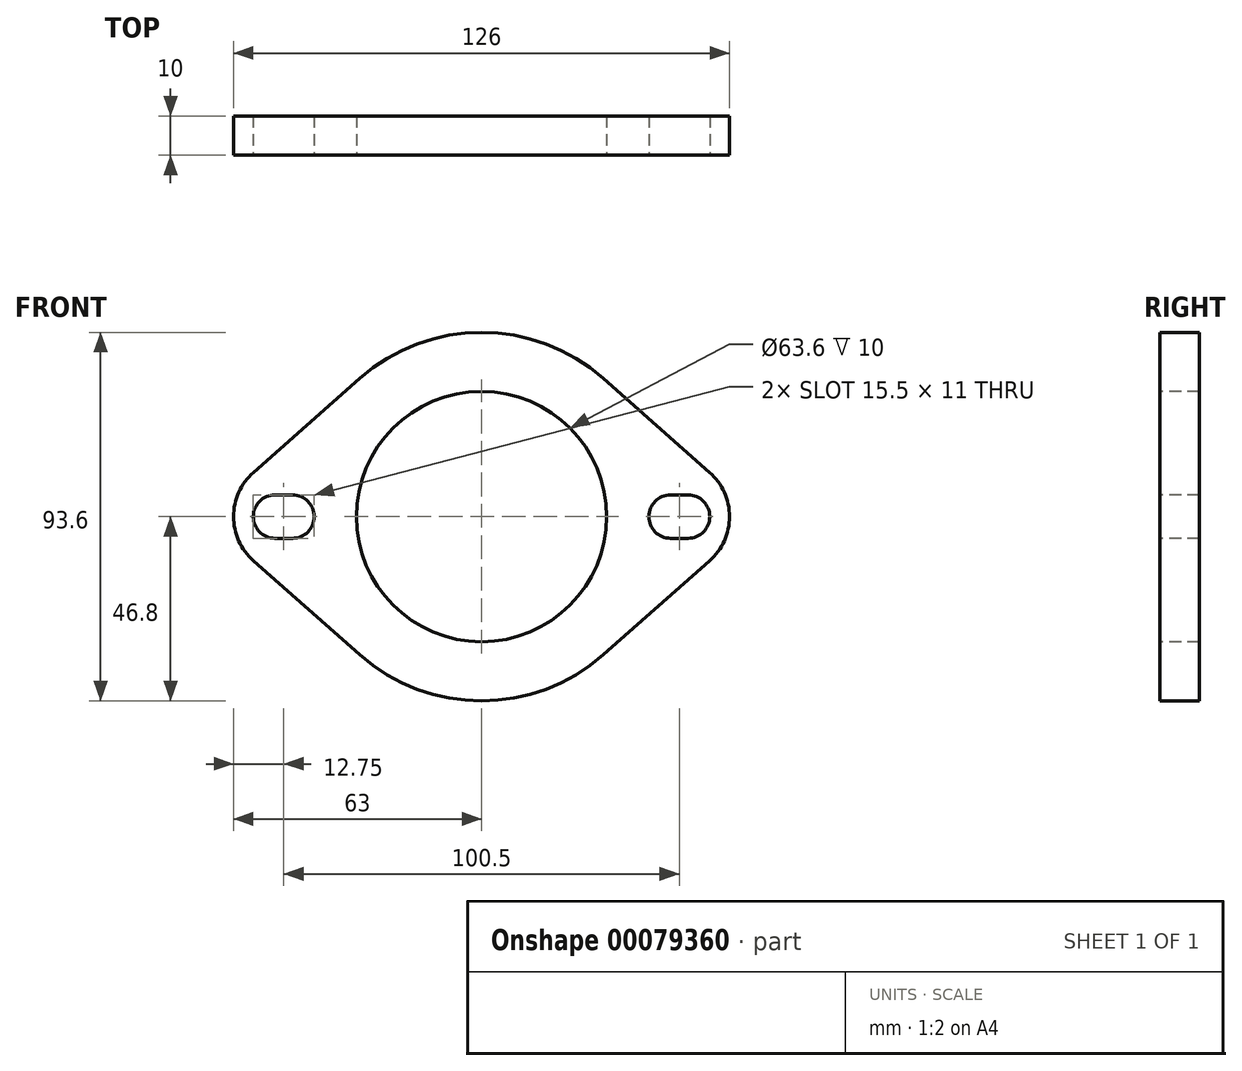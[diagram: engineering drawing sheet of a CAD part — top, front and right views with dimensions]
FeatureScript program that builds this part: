
annotation { "Feature Type Name" : "Feature", "Feature Type Description" : "" }
export const myFeature = defineFeature(function(context is Context, id is Id, definition is map)
    precondition{}
    {
        {
            var Q0;
            Q0=qCreatedBy(makeId("Front.planeOp"),FACE);
            var sketch = newSketch(context, id + "F0", { "sketchPlane" : qUnion([Q0])});
            skCircle(sketch, "E0", {"center": v(73, 56.8) * mm, "radius": 31.8 * mm});
            skArc(sketch, "E1", {"start": v(42, 21.74) * mm, "mid": v(73, 10) * mm, "end": v(104, 21.74) * mm});
            skArc(sketch, "E2", {"start": v(15.06, 68.04) * mm, "mid": v(10, 56.8) * mm, "end": v(15.06, 45.56) * mm});
            skArc(sketch, "E3", {"start": v(130.94, 45.56) * mm, "mid": v(136, 56.8) * mm, "end": v(130.94, 68.04) * mm});
            skLineSegment(sketch, "E4", {"start": v(15.06, 68.04) * mm, "end": v(42, 91.86) * mm});
            skLineSegment(sketch, "E5", {"start": v(15.06, 45.56) * mm, "end": v(42, 21.74) * mm});
            skLineSegment(sketch, "E6", {"start": v(130.94, 68.04) * mm, "end": v(104, 91.86) * mm});
            skLineSegment(sketch, "E7", {"start": v(130.94, 45.56) * mm, "end": v(104, 21.74) * mm});
            skArc(sketch, "E8.trimOffspring", {"start": v(104, 91.86) * mm, "mid": v(73, 103.6) * mm, "end": v(42, 91.86) * mm});
            skArc(sketch, "E9", {"start": v(25, 51.3) * mm, "mid": v(30.5, 56.8) * mm, "end": v(25, 62.3) * mm});
            skArc(sketch, "E10", {"start": v(20.5, 62.3) * mm, "mid": v(15, 56.8) * mm, "end": v(20.5, 51.3) * mm});
            skLineSegment(sketch, "E11", {"start": v(20.5, 51.3) * mm, "end": v(25, 51.3) * mm});
            skArc(sketch, "E12.MirrorCS", {"start": v(121, 51.3) * mm, "mid": v(115.5, 56.8) * mm, "end": v(121, 62.3) * mm});
            skArc(sketch, "E13.MirrorCS", {"start": v(125.5, 62.3) * mm, "mid": v(131, 56.8) * mm, "end": v(125.5, 51.3) * mm});
            skLineSegment(sketch, "E14", {"start": v(20.5, 62.3) * mm, "end": v(25, 62.3) * mm});
            skLineSegment(sketch, "E15", {"start": v(121, 62.3) * mm, "end": v(125.5, 62.3) * mm});
            skLineSegment(sketch, "E16", {"start": v(121, 51.3) * mm, "end": v(125.5, 51.3) * mm});
            skLineSegment(sketch, "E17", {"start": v(0, 0) * mm, "end": v(0, 82.13) * mm});
            skLineSegment(sketch, "E18", {"start": v(0, 0) * mm, "end": v(145.22, 0) * mm});
            skSolve(sketch);
        }
        {
            var Q0;
            Q0=makeQuery(id+"F0.imprint","IMPRINT",FACE,{"disambiguationData":[TD([[makeQuery(id+"F0.imprint","IMPRINT",EDGE,{"derivedFrom":sQuery(id+"F0.wireOp",EDGE,"E0")}),-1.0]])]});
            extrude(context, id + "F1", {"entities" : qUnion([Q0]), "oppositeDirection" : true, "depth" : 10 * mm});
        }
    });
